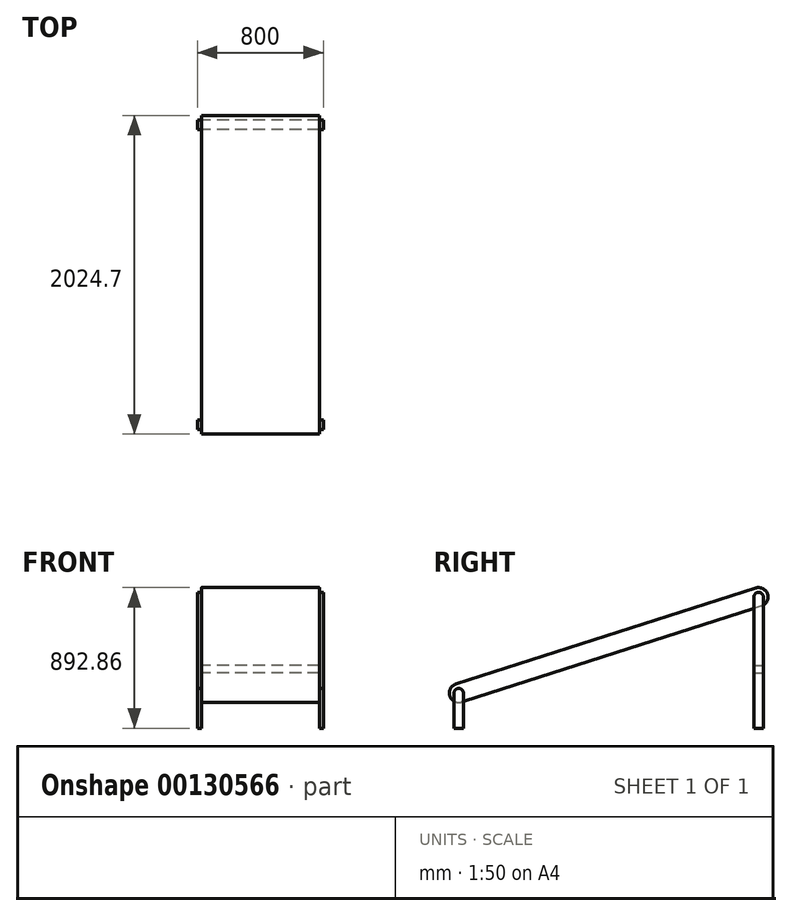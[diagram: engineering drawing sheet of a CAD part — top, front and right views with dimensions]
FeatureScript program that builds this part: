
annotation { "Feature Type Name" : "Feature", "Feature Type Description" : "" }
export const myFeature = defineFeature(function(context is Context, id is Id, definition is map)
    precondition{}
    {
        {
            var Q0;
            Q0=qCreatedBy(makeId("Right.planeOp"),FACE);
            var sketch = newSketch(context, id + "F0", { "sketchPlane" : qUnion([Q0])});
            skLineSegment(sketch, "E0", {"start": v(-970.65, 280) * mm, "end": v(-934.05, 165.72) * mm, "construction": true});
            skLineSegment(sketch, "E1", {"start": v(-970.65, 280) * mm, "end": v(934.05, 890) * mm});
            skLineSegment(sketch, "E2", {"start": v(970.65, 775.72) * mm, "end": v(934.05, 890) * mm, "construction": true});
            skLineSegment(sketch, "E3", {"start": v(970.65, 775.72) * mm, "end": v(-934.05, 165.72) * mm});
            skArc(sketch, "E4", {"start": v(-970.65, 280) * mm, "mid": v(-1009.5, 204.56) * mm, "end": v(-934.05, 165.72) * mm});
            skArc(sketch, "E5", {"start": v(934.05, 890) * mm, "mid": v(1009.5, 851.16) * mm, "end": v(970.65, 775.72) * mm});
            skLineSegment(sketch, "E6", {"start": v(-952.35, 222.86) * mm, "end": v(952.35, 832.86) * mm, "construction": true});
            skPoint(sketch, "E7", {"position": v(0, 527.86) * mm});
            skSolve(sketch);
        }
        {
            var Q0;
            Q0 = qSketchRegion(id + "F0", true);
            extrude(context, id + "F1", {"entities" : qUnion([Q0]), "endBound" : BoundingType.SYMMETRIC, "depth" : 750 * mm});
        }
        {
            var Q0;
            Q0=makeQuery(id+"F1.opExtrude","CAP_FACE",FACE,{"disambiguationData":[OSD([sQuery(id+"F0.wireOp",EDGE,"E1"),sQuery(id+"F0.wireOp",EDGE,"E3"),sQuery(id+"F0.wireOp",EDGE,"E4"),sQuery(id+"F0.wireOp",EDGE,"E5")])],"isStart":false});
            var sketch = newSketch(context, id + "F2", { "sketchPlane" : qUnion([Q0])});
            skLineSegment(sketch, "E8.top", {"start": v(-982.35, 0) * mm, "end": v(-922.35, 0) * mm});
            skLineSegment(sketch, "E8.left", {"start": v(-982.35, 222.86) * mm, "end": v(-982.35, 0) * mm});
            skLineSegment(sketch, "E8.right", {"start": v(-922.35, 222.86) * mm, "end": v(-922.35, 0) * mm});
            skLineSegment(sketch, "E9.top", {"start": v(922.35, 0) * mm, "end": v(982.35, 0) * mm});
            skLineSegment(sketch, "E9.left", {"start": v(922.35, 832.86) * mm, "end": v(922.35, 0) * mm});
            skLineSegment(sketch, "E10", {"start": v(982.35, 0) * mm, "end": v(982.35, 832.86) * mm});
            skCircle(sketch, "E11", {"center": v(-952.35, 222.86) * mm, "radius": 30 * mm, "construction": true});
            skPoint(sketch, "E11.first.point", {"position": v(-982.35, 222.86) * mm});
            skPoint(sketch, "E11.third.point", {"position": v(-922.35, 222.86) * mm});
            skCircle(sketch, "E12", {"center": v(952.35, 832.86) * mm, "radius": 30 * mm, "construction": true});
            skArc(sketch, "E13", {"start": v(-982.35, 222.86) * mm, "mid": v(-952.35, 252.86) * mm, "end": v(-922.35, 222.86) * mm});
            skArc(sketch, "E14", {"start": v(922.35, 832.86) * mm, "mid": v(952.35, 862.86) * mm, "end": v(982.35, 832.86) * mm});
            skSolve(sketch);
        }
        {
            var Q0;
            Q0 = qSketchRegion(id + "F2", true);
            extrude(context, id + "F3", {"entities" : qUnion([Q0]), "depth" : 25 * mm});
        }
        {
            var Q0;
            Q0=makeQuery(id+"F3.opExtrude","SWEPT_BODY",BODY,{"disambiguationData":[OSD([sQuery(id+"F2.wireOp",EDGE,"E8.bottom"),sQuery(id+"F2.wireOp",EDGE,"E8.top"),sQuery(id+"F2.wireOp",EDGE,"E8.left"),sQuery(id+"F2.wireOp",EDGE,"E8.right")])]});
            var Q1;
            Q1=makeQuery(id+"F3.opExtrude","SWEPT_BODY",BODY,{"disambiguationData":[OSD([sQuery(id+"F2.wireOp",EDGE,"E9.top"),sQuery(id+"F2.wireOp",EDGE,"E9.left"),sQuery(id+"F2.wireOp",EDGE,"E10"),sQuery(id+"F2.wireOp",EDGE,"gYBjOb9H-vqH4-L1zV-pU83-aWa8Uyf1uBEf")])]});
            var Q2;
            Q2=qCreatedBy(makeId("Right.planeOp"),FACE);
            mirror(context, id + "F4", {"operationType" : NewBodyOperationType.ADD, "entities" : qUnion([Q0, Q1]), "mirrorPlane" : qUnion([Q2])});
        }
        {
            var Q0;
            Q0=makeQuery(id+"F4.opPattern","COPY",FACE,{"derivedFrom":makeQuery(id+"F3.opExtrude","CAP_FACE",FACE,{"disambiguationData":[OSD([sQuery(id+"F2.wireOp",EDGE,"E9.top"),sQuery(id+"F2.wireOp",EDGE,"E9.left"),sQuery(id+"F2.wireOp",EDGE,"E10"),sQuery(id+"F2.wireOp",EDGE,"gYBjOb9H-vqH4-L1zV-pU83-aWa8Uyf1uBEf")])],"isStart":true}),"instanceName":"1"});
            var sketch = newSketch(context, id + "F5", { "sketchPlane" : qUnion([Q0])});
            skLineSegment(sketch, "E15.bottom", {"start": v(922.35, 400) * mm, "end": v(982.35, 400) * mm});
            skLineSegment(sketch, "E15.top", {"start": v(922.35, 350) * mm, "end": v(982.35, 350) * mm});
            skLineSegment(sketch, "E15.left", {"start": v(922.35, 400) * mm, "end": v(922.35, 350) * mm});
            skLineSegment(sketch, "E15.right", {"start": v(982.35, 400) * mm, "end": v(982.35, 350) * mm});
            skSolve(sketch);
        }
        {
            var Q0;
            Q0 = qSketchRegion(id + "F5", true);
            var Q1;
            Q1=makeQuery(id+"F3.opExtrude","CAP_FACE",FACE,{"disambiguationData":[OSD([sQuery(id+"F2.wireOp",EDGE,"E9.top"),sQuery(id+"F2.wireOp",EDGE,"E9.left"),sQuery(id+"F2.wireOp",EDGE,"E10"),sQuery(id+"F2.wireOp",EDGE,"gYBjOb9H-vqH4-L1zV-pU83-aWa8Uyf1uBEf")])],"isStart":true});
            extrude(context, id + "F6", {"entities" : qUnion([Q0]), "operationType" : NewBodyOperationType.ADD, "endBound" : BoundingType.UP_TO_SURFACE, "endBoundEntityFace" : qUnion([Q1]), "depth" : 25 * mm});
        }
    });
